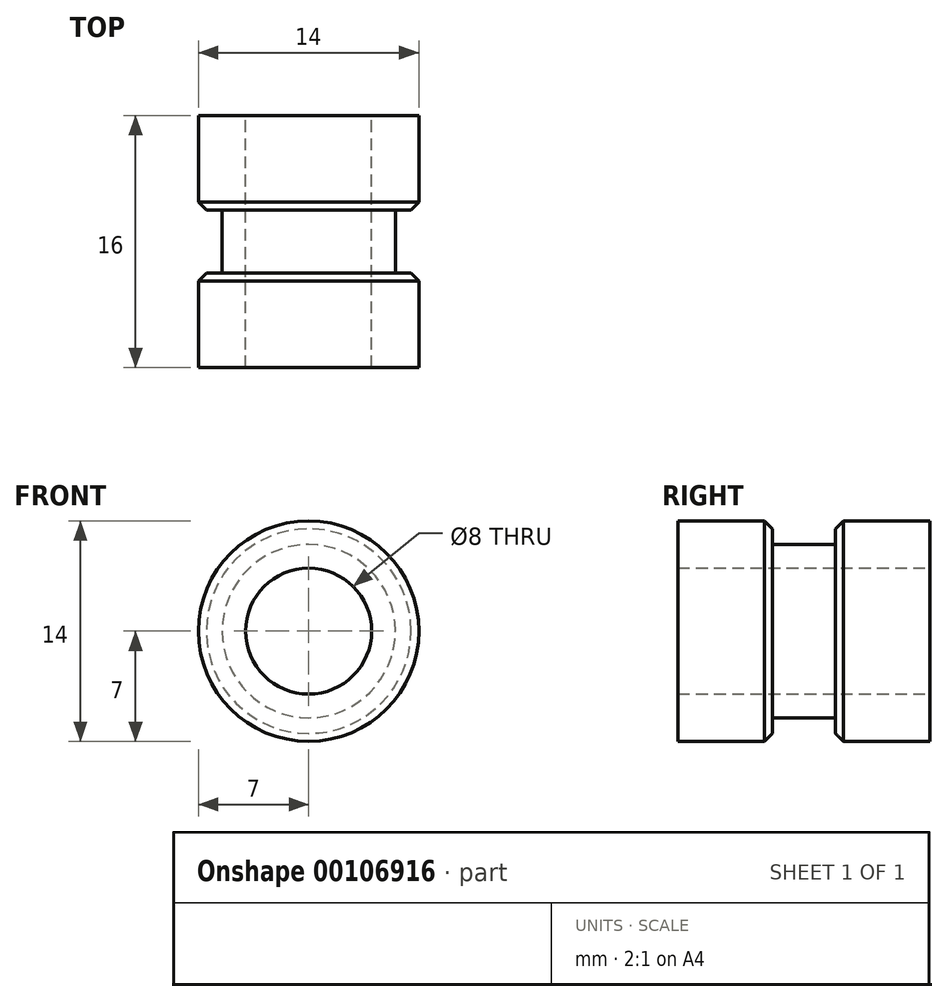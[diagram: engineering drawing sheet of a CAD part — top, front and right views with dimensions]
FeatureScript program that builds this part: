
annotation { "Feature Type Name" : "Feature", "Feature Type Description" : "" }
export const myFeature = defineFeature(function(context is Context, id is Id, definition is map)
    precondition{}
    {
        {
            var Q0;
            Q0=qCreatedBy(makeId("Front.planeOp"),FACE);
            var sketch = newSketch(context, id + "F0", { "sketchPlane" : qUnion([Q0])});
            skCircle(sketch, "E0", {"center": v(0, 0) * mm, "radius": 7 * mm});
            skCircle(sketch, "E1", {"center": v(0, 0) * mm, "radius": 4 * mm});
            skSolve(sketch);
        }
        {
            var Q0;
            Q0 = qSketchRegion(id + "F0", true);
            extrude(context, id + "F1", {"entities" : qUnion([Q0]), "depth" : 6 * mm});
        }
        {
            var Q0;
            Q0=makeQuery(id+"F1.opExtrude","CAP_FACE",FACE,{"disambiguationData":[OSD([sQuery(id+"F0.wireOp",EDGE,"E0"),sQuery(id+"F0.wireOp",EDGE,"E1")])],"isStart":false});
            var sketch = newSketch(context, id + "F2", { "sketchPlane" : qUnion([Q0])});
            skCircle(sketch, "E2", {"center": v(0, 0) * mm, "radius": 5.5 * mm});
            skCircle(sketch, "E3", {"center": v(0, 0) * mm, "radius": 4 * mm});
            skSolve(sketch);
        }
        {
            var Q0;
            Q0 = qSketchRegion(id + "F2", true);
            extrude(context, id + "F3", {"entities" : qUnion([Q0]), "operationType" : NewBodyOperationType.ADD, "depth" : 4 * mm});
        }
        {
            var Q0;
            Q0=makeQuery(id+"F3.opExtrude","CAP_FACE",FACE,{"disambiguationData":[OSD([sQuery(id+"F2.wireOp",EDGE,"E2"),sQuery(id+"F2.wireOp",EDGE,"E3")])],"isStart":false});
            var sketch = newSketch(context, id + "F4", { "sketchPlane" : qUnion([Q0])});
            skCircle(sketch, "E4", {"center": v(0, 0) * mm, "radius": 7 * mm});
            skCircle(sketch, "E5", {"center": v(0, 0) * mm, "radius": 4 * mm});
            skSolve(sketch);
        }
        {
            var Q0;
            Q0 = qSketchRegion(id + "F4", true);
            extrude(context, id + "F5", {"entities" : qUnion([Q0]), "operationType" : NewBodyOperationType.ADD, "depth" : 6 * mm});
        }
        {
            var Q0;
            Q0=makeQuery(id+"F1.opExtrude","CAP_EDGE",EDGE,{"disambiguationData":[OSD([sQuery(id+"F0.wireOp",EDGE,"E0")])],"isStart":false});
            var Q1;
            Q1=makeQuery(id+"F5.opExtrude","CAP_EDGE",EDGE,{"disambiguationData":[OSD([sQuery(id+"F4.wireOp",EDGE,"E4")])],"isStart":true});
            chamfer(context, id + "F6", {"entities" : qUnion([Q0, Q1]), "width" : .5 * mm, "tangentPropagation" : true});
        }
    });
